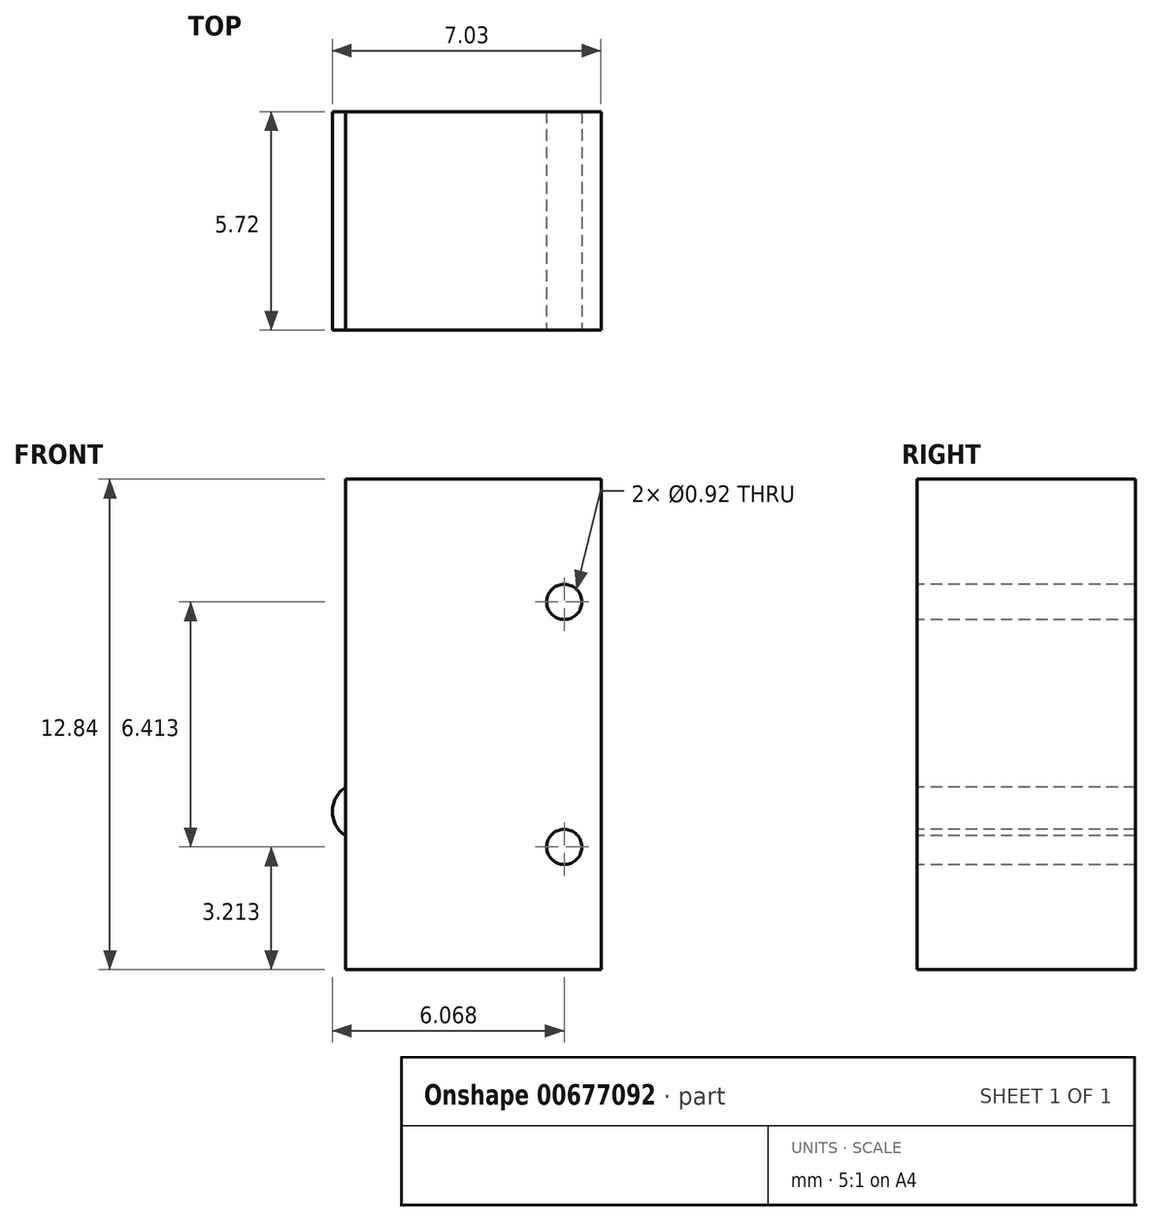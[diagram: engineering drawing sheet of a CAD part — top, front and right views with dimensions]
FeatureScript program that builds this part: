
annotation { "Feature Type Name" : "Feature", "Feature Type Description" : "" }
export const myFeature = defineFeature(function(context is Context, id is Id, definition is map)
    precondition{}
    {
        {
            var Q0;
            Q0=qCreatedBy(makeId("Right.planeOp"),FACE);
            var sketch = newSketch(context, id + "F0", { "sketchPlane" : qUnion([Q0])});
            skLineSegment(sketch, "E0.bottom", {"start": v(2.86, 6.42) * mm, "end": v(-2.86, 6.42) * mm});
            skLineSegment(sketch, "E0.top", {"start": v(2.86, -6.42) * mm, "end": v(-2.86, -6.42) * mm});
            skLineSegment(sketch, "E0.left", {"start": v(2.86, 6.42) * mm, "end": v(2.86, -6.42) * mm});
            skLineSegment(sketch, "E0.right", {"start": v(-2.86, 6.42) * mm, "end": v(-2.86, -6.42) * mm});
            skPoint(sketch, "E0.middle", {"position": v(0, 0) * mm});
            skSolve(sketch);
        }
        {
            var Q0;
            Q0 = qSketchRegion(id + "F0", true);
            extrude(context, id + "F1", {"entities" : qUnion([Q0]), "depth" : 6.7 * mm, "offsetDistance" : 25.4 * mm});
        }
        {
            var Q0;
            Q0=makeQuery(id+"F1.opExtrude","SWEPT_FACE",FACE,{"disambiguationData":[OSD([sQuery(id+"F0.wireOp",EDGE,"E0.right")])]});
            var sketch = newSketch(context, id + "F2", { "sketchPlane" : qUnion([Q0])});
            skArc(sketch, "E1", {"start": v(0, -1.64) * mm, "mid": v(-0.34, -2.28) * mm, "end": v(0, -2.91) * mm});
            skLineSegment(sketch, "E2", {"start": v(0, -2.91) * mm, "end": v(0, -1.64) * mm});
            skSolve(sketch);
        }
        {
            var Q0;
            Q0 = qSketchRegion(id + "F2", true);
            var Q1;
            Q1=makeQuery(id+"F1.opExtrude","SWEPT_FACE",FACE,{"disambiguationData":[OSD([sQuery(id+"F0.wireOp",EDGE,"E0.left")])]});
            extrude(context, id + "F3", {"entities" : qUnion([Q0]), "endBound" : BoundingType.UP_TO_SURFACE, "oppositeDirection" : true, "depth" : 25.4 * mm, "endBoundEntityFace" : qUnion([Q1]), "offsetDistance" : 25.4 * mm});
        }
        {
            var Q0;
            Q0=makeQuery(id+"F1.opExtrude","SWEPT_FACE",FACE,{"disambiguationData":[OSD([sQuery(id+"F0.wireOp",EDGE,"E0.right")])]});
            var sketch = newSketch(context, id + "F4", { "sketchPlane" : qUnion([Q0])});
            skLineSegment(sketch, "E3", {"start": v(6.7, 0) * mm, "end": v(5.73, 0) * mm});
            skLineSegment(sketch, "E4", {"start": v(5.73, -3.2) * mm, "end": v(5.73, 3.2) * mm, "construction": true});
            skCircle(sketch, "E5", {"center": v(5.73, 3.2) * mm, "radius": 0.46 * mm});
            skCircle(sketch, "E6", {"center": v(5.73, -3.2) * mm, "radius": 0.46 * mm});
            skSolve(sketch);
        }
        {
            var Q0;
            Q0 = qSketchRegion(id + "F4", true);
            extrude(context, id + "F5", {"entities" : qUnion([Q0]), "operationType" : NewBodyOperationType.REMOVE, "endBound" : BoundingType.UP_TO_NEXT, "oppositeDirection" : true, "depth" : 25.4 * mm, "offsetDistance" : 25.4 * mm});
        }
    });
